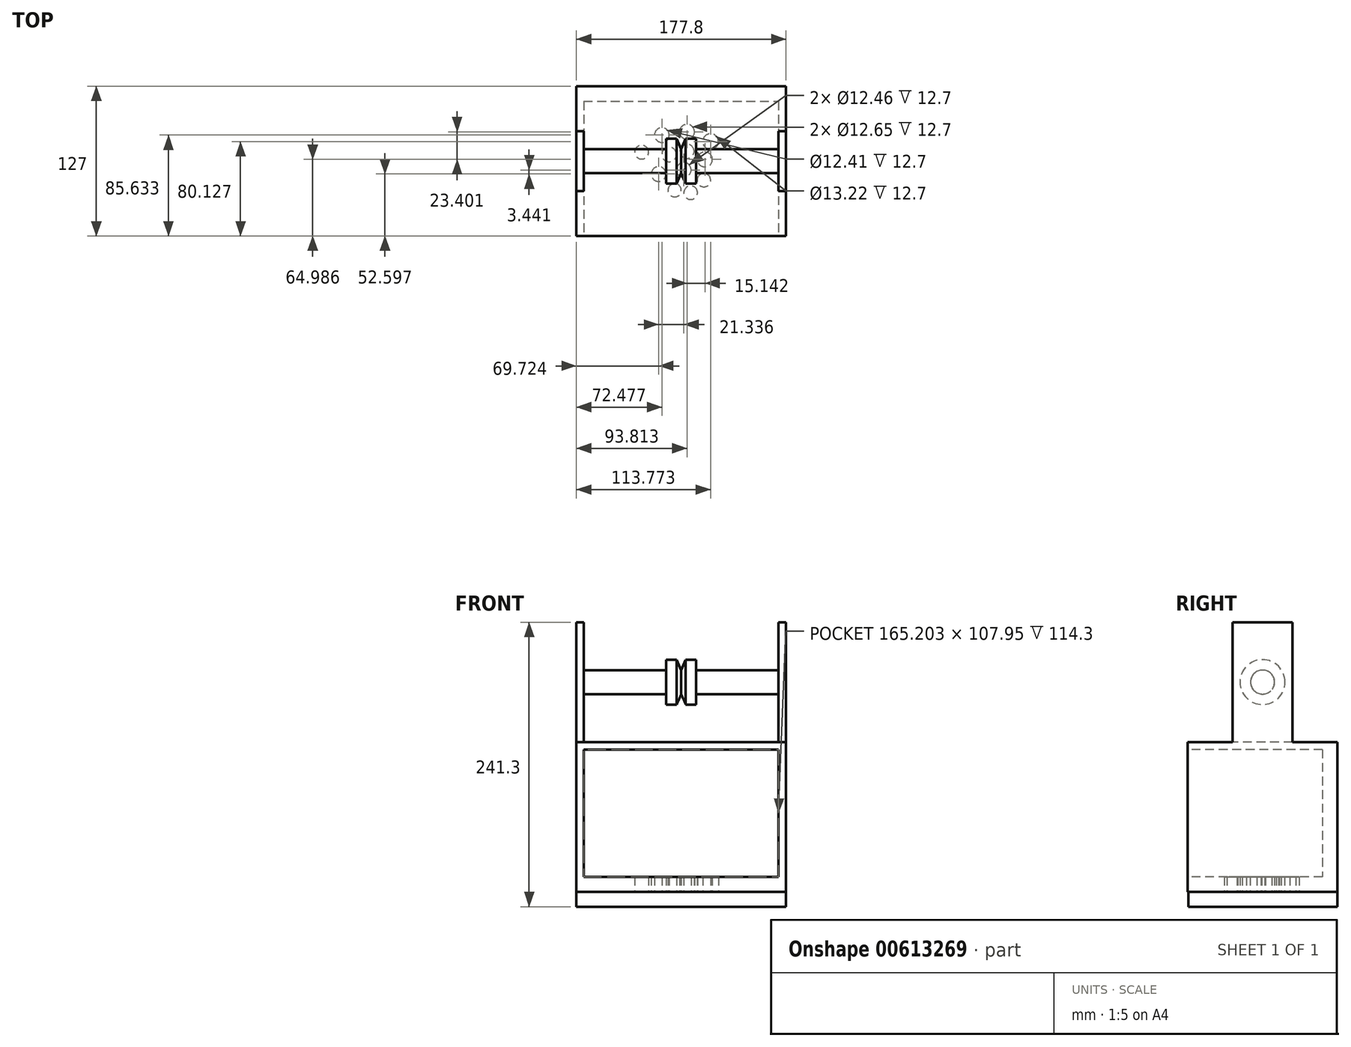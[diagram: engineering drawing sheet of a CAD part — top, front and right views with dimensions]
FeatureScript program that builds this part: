
annotation { "Feature Type Name" : "Feature", "Feature Type Description" : "" }
export const myFeature = defineFeature(function(context is Context, id is Id, definition is map)
    precondition{}
    {
        {
            var Q0;
            Q0=qCreatedBy(makeId("Front.planeOp"),FACE);
            var sketch = newSketch(context, id + "F0", { "sketchPlane" : qUnion([Q0])});
            skLineSegment(sketch, "E0", {"start": v(0, 0) * mm, "end": v(177.8, 0) * mm});
            skLineSegment(sketch, "E1", {"start": v(177.8, 0) * mm, "end": v(177.8, 228.6) * mm});
            skLineSegment(sketch, "E2", {"start": v(177.8, 228.6) * mm, "end": v(0, 228.6) * mm});
            skLineSegment(sketch, "E3", {"start": v(0, 228.6) * mm, "end": v(0, 0) * mm});
            skSolve(sketch);
        }
        {
            var Q0;
            Q0 = qSketchRegion(id + "F0", true);
            extrude(context, id + "F1", {"entities" : qUnion([Q0]), "depth" : 127 * mm, "offsetDistance" : 25.4 * mm});
        }
        {
            var Q0;
            Q0=makeQuery(id+"F1.opExtrude","SWEPT_FACE",FACE,{"disambiguationData":[OSD([sQuery(id+"F0.wireOp",EDGE,"E1")])]});
            var sketch = newSketch(context, id + "F2", { "sketchPlane" : qUnion([Q0])});
            skLineSegment(sketch, "E4.bottom", {"start": v(-127, 228.6) * mm, "end": v(-88.9, 228.6) * mm});
            skLineSegment(sketch, "E4.top", {"start": v(-127, 127) * mm, "end": v(-88.9, 127) * mm});
            skLineSegment(sketch, "E4.left", {"start": v(-127, 228.6) * mm, "end": v(-127, 127) * mm});
            skLineSegment(sketch, "E4.right", {"start": v(-88.9, 228.6) * mm, "end": v(-88.9, 127) * mm});
            skSolve(sketch);
        }
        {
            var Q0;
            Q0=makeQuery(id+"F2.imprint","IMPRINT",FACE,{"disambiguationData":[TD([[makeQuery(id+"F2.imprint","IMPRINT",EDGE,{"derivedFrom":sQuery(id+"F2.wireOp",EDGE,"E4.bottom")}),-1.0]])]});
            extrude(context, id + "F3", {"entities" : qUnion([Q0]), "operationType" : NewBodyOperationType.REMOVE, "oppositeDirection" : true, "depth" : 177.8 * mm, "offsetDistance" : 25.4 * mm});
        }
        {
            var Q0;
            Q0=makeQuery(id+"F1.opExtrude","SWEPT_FACE",FACE,{"disambiguationData":[OSD([sQuery(id+"F0.wireOp",EDGE,"E1")])]});
            var sketch = newSketch(context, id + "F4", { "sketchPlane" : qUnion([Q0])});
            skLineSegment(sketch, "E5.bottom", {"start": v(0, 228.6) * mm, "end": v(-38.1, 228.6) * mm});
            skLineSegment(sketch, "E5.top", {"start": v(0, 127) * mm, "end": v(-38.1, 127) * mm});
            skLineSegment(sketch, "E5.left", {"start": v(0, 228.6) * mm, "end": v(0, 127) * mm});
            skLineSegment(sketch, "E5.right", {"start": v(-38.1, 228.6) * mm, "end": v(-38.1, 127) * mm});
            skSolve(sketch);
        }
        {
            var Q0;
            Q0=makeQuery(id+"F4.imprint","IMPRINT",FACE,{"disambiguationData":[TD([[makeQuery(id+"F4.imprint","IMPRINT",EDGE,{"derivedFrom":sQuery(id+"F4.wireOp",EDGE,"E5.bottom")}),-1.0]])]});
            extrude(context, id + "F5", {"entities" : qUnion([Q0]), "operationType" : NewBodyOperationType.REMOVE, "oppositeDirection" : true, "depth" : 177.8 * mm, "offsetDistance" : 25.4 * mm});
        }
        {
            var Q0;
            Q0=makeQuery(id+"F1.opExtrude","SWEPT_FACE",FACE,{"disambiguationData":[OSD([sQuery(id+"F0.wireOp",EDGE,"E3")])]});
            var sketch = newSketch(context, id + "F6", { "sketchPlane" : qUnion([Q0])});
            skCircle(sketch, "E6", {"center": v(61.07, 211.22) * mm, "radius": 6.2 * mm});
            skSolve(sketch);
        }
        {
            var Q0;
            Q0=makeQuery(id+"F6.imprint","IMPRINT",FACE,{"disambiguationData":[TD([[makeQuery(id+"F6.imprint","IMPRINT",EDGE,{"derivedFrom":sQuery(id+"F6.wireOp",EDGE,"E6")}),1.0]])]});
            extrude(context, id + "F7", {"entities" : qUnion([Q0]), "operationType" : NewBodyOperationType.ADD, "oppositeDirection" : true, "depth" : 177.8 * mm, "offsetDistance" : 25.4 * mm});
        }
        {
            var Q0;
            Q0=makeQuery(id+"F1.opExtrude","SWEPT_FACE",FACE,{"disambiguationData":[OSD([sQuery(id+"F0.wireOp",EDGE,"E2")])]});
            var sketch = newSketch(context, id + "F8", { "sketchPlane" : qUnion([Q0])});
            skLineSegment(sketch, "E7", {"start": v(177.8, -38.1) * mm, "end": v(171.45, -38.1) * mm});
            skLineSegment(sketch, "E8", {"start": v(171.45, -38.1) * mm, "end": v(171.45, -88.9) * mm});
            skLineSegment(sketch, "E9", {"start": v(171.45, -88.9) * mm, "end": v(177.8, -88.9) * mm});
            skLineSegment(sketch, "E10", {"start": v(177.8, -88.9) * mm, "end": v(177.8, -38.1) * mm});
            skLineSegment(sketch, "E11", {"start": v(171.45, -38.1) * mm, "end": v(177.8, -38.1) * mm});
            skLineSegment(sketch, "E12", {"start": v(0, -88.9) * mm, "end": v(6.35, -88.9) * mm});
            skLineSegment(sketch, "E13", {"start": v(6.35, -88.9) * mm, "end": v(6.35, -38.1) * mm});
            skLineSegment(sketch, "E14", {"start": v(6.35, -38.1) * mm, "end": v(0, -38.1) * mm});
            skLineSegment(sketch, "E15", {"start": v(0, -38.1) * mm, "end": v(0, -88.9) * mm});
            skSolve(sketch);
        }
        {
            var Q0;
            {var subQ0=sQuery(id+"F8.wireOp",EDGE,"E8");Q0=makeQuery(id+"F8.imprint","IMPRINT",FACE,{"disambiguationData":[TD([[makeQuery(id+"F8.imprint","IMPRINT",EDGE,{"derivedFrom":subQ0}),-1.0]])]});}
            extrude(context, id + "F9", {"entities" : qUnion([Q0]), "operationType" : NewBodyOperationType.REMOVE, "oppositeDirection" : true, "depth" : 101.6 * mm, "offsetDistance" : 25.4 * mm});
        }
        {
            var Q0;
            Q0=makeQuery(id+"F1.opExtrude","SWEPT_FACE",FACE,{"disambiguationData":[OSD([sQuery(id+"F0.wireOp",EDGE,"E1")])]});
            var sketch = newSketch(context, id + "F10", { "sketchPlane" : qUnion([Q0])});
            skLineSegment(sketch, "E16", {"start": v(-63.5, 228.6) * mm, "end": v(-63.5, 128.6) * mm});
            skLineSegment(sketch, "E17", {"start": v(-88.9, 177.8) * mm, "end": v(-38.1, 177.8) * mm});
            skCircle(sketch, "E18", {"center": v(-63.5, 177.8) * mm, "radius": 10.2 * mm});
            skSolve(sketch);
        }
        {
            var Q0;
            {var subQ0=sQuery(id+"F10.wireOp",EDGE,"E18");var subQ1=sQuery(id+"F10.wireOp",EDGE,"E16");var subQ2=makeQuery(id+"F10.imprint","INTERSECT",VERTEX,{"disambiguationData":[OD(1.0)],"derivedFrom":[subQ1,subQ0]});Q0=makeQuery(id+"F10.imprint","IMPRINT",FACE,{"disambiguationData":[TD([[makeQuery(id+"F10.imprint","IMPRINT",EDGE,{"disambiguationData":[TD([[subQ2,-1.0]])],"derivedFrom":subQ1}),-1.0]])]});}
            var Q1;
            {var subQ0=sQuery(id+"F10.wireOp",EDGE,"E18");var subQ1=sQuery(id+"F10.wireOp",EDGE,"E16");var subQ2=makeQuery(id+"F10.imprint","INTERSECT",VERTEX,{"disambiguationData":[OD(0.0)],"derivedFrom":[subQ1,subQ0]});Q1=makeQuery(id+"F10.imprint","IMPRINT",FACE,{"disambiguationData":[TD([[makeQuery(id+"F10.imprint","IMPRINT",EDGE,{"disambiguationData":[TD([[subQ2,1.0]])],"derivedFrom":subQ1}),-1.0]])]});}
            var Q2;
            {var subQ0=sQuery(id+"F10.wireOp",EDGE,"E18");var subQ1=sQuery(id+"F10.wireOp",EDGE,"E16");var subQ2=makeQuery(id+"F10.imprint","INTERSECT",VERTEX,{"disambiguationData":[OD(0.0)],"derivedFrom":[subQ1,subQ0]});Q2=makeQuery(id+"F10.imprint","IMPRINT",FACE,{"disambiguationData":[TD([[makeQuery(id+"F10.imprint","IMPRINT",EDGE,{"disambiguationData":[TD([[subQ2,1.0]])],"derivedFrom":subQ1}),1.0]])]});}
            var Q3;
            {var subQ0=sQuery(id+"F10.wireOp",EDGE,"E18");var subQ1=sQuery(id+"F10.wireOp",EDGE,"E16");var subQ2=makeQuery(id+"F10.imprint","INTERSECT",VERTEX,{"disambiguationData":[OD(1.0)],"derivedFrom":[subQ1,subQ0]});Q3=makeQuery(id+"F10.imprint","IMPRINT",FACE,{"disambiguationData":[TD([[makeQuery(id+"F10.imprint","IMPRINT",EDGE,{"disambiguationData":[TD([[subQ2,-1.0]])],"derivedFrom":subQ1}),1.0]])]});}
            extrude(context, id + "F11", {"entities" : qUnion([Q0, Q1, Q2, Q3]), "operationType" : NewBodyOperationType.ADD, "oppositeDirection" : true, "depth" : 174.5 * mm, "offsetDistance" : 25.4 * mm});
        }
        {
            var Q0;
            Q0=makeQuery(id+"F1.opExtrude","CAP_FACE",FACE,{"disambiguationData":[OSD([sQuery(id+"F0.wireOp",EDGE,"E0"),sQuery(id+"F0.wireOp",EDGE,"E1"),sQuery(id+"F0.wireOp",EDGE,"E2"),sQuery(id+"F0.wireOp",EDGE,"E3")])],"isStart":false});
            var sketch = newSketch(context, id + "F12", { "sketchPlane" : qUnion([Q0])});
            skLineSegment(sketch, "E19", {"start": v(0, 127) * mm, "end": v(0, 120.65) * mm});
            skLineSegment(sketch, "E20", {"start": v(0, 120.65) * mm, "end": v(177.8, 120.65) * mm});
            skLineSegment(sketch, "E21", {"start": v(177.8, 120.65) * mm, "end": v(177.8, 127) * mm});
            skLineSegment(sketch, "E22", {"start": v(177.8, 127) * mm, "end": v(0, 127) * mm});
            skLineSegment(sketch, "E23", {"start": v(0, 0) * mm, "end": v(0, 12.7) * mm});
            skLineSegment(sketch, "E24", {"start": v(0, 12.7) * mm, "end": v(177.8, 12.7) * mm});
            skLineSegment(sketch, "E25", {"start": v(177.8, 12.7) * mm, "end": v(177.8, 0) * mm});
            skLineSegment(sketch, "E26", {"start": v(177.8, 0) * mm, "end": v(0, 0) * mm});
            skLineSegment(sketch, "E27", {"start": v(171.35, 127) * mm, "end": v(171.35, 12.7) * mm});
            skLineSegment(sketch, "E28", {"start": v(6.15, 127) * mm, "end": v(6.15, 12.7) * mm});
            skSolve(sketch);
        }
        {
            var Q0;
            {var subQ0=sQuery(id+"F12.wireOp",EDGE,"E28");var subQ1=sQuery(id+"F12.wireOp",EDGE,"E20");var subQ2=makeQuery(id+"F12.imprint","INTERSECT",VERTEX,{"derivedFrom":[subQ1,subQ0]});Q0=makeQuery(id+"F12.imprint","IMPRINT",FACE,{"disambiguationData":[TD([[makeQuery(id+"F12.imprint","IMPRINT",EDGE,{"disambiguationData":[TD([[subQ2,-1.0]])],"derivedFrom":subQ1}),-1.0]])]});}
            extrude(context, id + "F13", {"entities" : qUnion([Q0]), "operationType" : NewBodyOperationType.REMOVE, "oppositeDirection" : true, "depth" : 114.3 * mm, "offsetDistance" : 25.4 * mm});
        }
        {
            var Q0;
            Q0=makeQuery(id+"F1.opExtrude","SWEPT_FACE",FACE,{"disambiguationData":[OSD([sQuery(id+"F0.wireOp",EDGE,"E0")])]});
            var sketch = newSketch(context, id + "F14", { "sketchPlane" : qUnion([Q0])});
            skSolve(sketch);
        }
        {
            var Q0;
            {var subQ0=sQuery(id+"F0.wireOp",EDGE,"E0");Q0=makeQuery(id+"F14.imprint","IMPRINT",FACE,{"disambiguationData":[TD([[makeQuery(id+"F14.imprint","IMPRINT",EDGE,{"derivedFrom":makeQuery(id+"F1.opExtrude","CAP_EDGE",EDGE,{"disambiguationData":[OSD([subQ0])],"isStart":true})}),1.0]])]});}
            var sketch = newSketch(context, id + "F15", { "sketchPlane" : qUnion([Q0])});
            skCircle(sketch, "E29", {"center": v(83.32, 88.2) * mm, "radius": 5.6 * mm});
            skSolve(sketch);
        }
        {
            var Q0;
            Q0 = qSketchRegion(id + "F15", true);
            extrude(context, id + "F16", {"entities" : qUnion([Q0]), "operationType" : NewBodyOperationType.REMOVE, "oppositeDirection" : true, "depth" : 25.4 * mm, "offsetDistance" : 25.4 * mm});
        }
        {
            var Q0;
            {var subQ0=sQuery(id+"F0.wireOp",EDGE,"E0");Q0=makeQuery(id+"F14.imprint","IMPRINT",FACE,{"disambiguationData":[TD([[makeQuery(id+"F14.imprint","IMPRINT",EDGE,{"derivedFrom":makeQuery(id+"F1.opExtrude","CAP_EDGE",EDGE,{"disambiguationData":[OSD([subQ0])],"isStart":true})}),1.0]])]});}
            var sketch = newSketch(context, id + "F17", { "sketchPlane" : qUnion([Q0])});
            skCircle(sketch, "E30", {"center": v(108.1, 79.6) * mm, "radius": 5.68 * mm});
            skSolve(sketch);
        }
        {
            var Q0;
            Q0 = qSketchRegion(id + "F17", true);
            extrude(context, id + "F18", {"entities" : qUnion([Q0]), "operationType" : NewBodyOperationType.REMOVE, "oppositeDirection" : true, "depth" : 25.4 * mm, "offsetDistance" : 25.4 * mm});
        }
        {
            var Q0;
            {var subQ0=sQuery(id+"F0.wireOp",EDGE,"E0");Q0=makeQuery(id+"F14.imprint","IMPRINT",FACE,{"disambiguationData":[TD([[makeQuery(id+"F14.imprint","IMPRINT",EDGE,{"derivedFrom":makeQuery(id+"F1.opExtrude","CAP_EDGE",EDGE,{"disambiguationData":[OSD([subQ0])],"isStart":true})}),1.0]])]});}
            var sketch = newSketch(context, id + "F19", { "sketchPlane" : qUnion([Q0])});
            skCircle(sketch, "E31", {"center": v(91.06, 70.96) * mm, "radius": 6.23 * mm});
            skSolve(sketch);
        }
        {
            var Q0;
            Q0 = qSketchRegion(id + "F19", true);
            extrude(context, id + "F20", {"entities" : qUnion([Q0]), "operationType" : NewBodyOperationType.REMOVE, "oppositeDirection" : true, "depth" : 25.4 * mm, "offsetDistance" : 25.4 * mm});
        }
        {
            var Q0;
            {var subQ0=sQuery(id+"F0.wireOp",EDGE,"E0");Q0=makeQuery(id+"F14.imprint","IMPRINT",FACE,{"disambiguationData":[TD([[makeQuery(id+"F14.imprint","IMPRINT",EDGE,{"derivedFrom":makeQuery(id+"F1.opExtrude","CAP_EDGE",EDGE,{"disambiguationData":[OSD([subQ0])],"isStart":true})}),1.0]])]});}
            var sketch = newSketch(context, id + "F21", { "sketchPlane" : qUnion([Q0])});
            skCircle(sketch, "E32", {"center": v(69.72, 74.4) * mm, "radius": 6.23 * mm});
            skSolve(sketch);
        }
        {
            var Q0;
            Q0 = qSketchRegion(id + "F21", true);
            extrude(context, id + "F22", {"entities" : qUnion([Q0]), "operationType" : NewBodyOperationType.REMOVE, "oppositeDirection" : true, "depth" : 25.4 * mm, "offsetDistance" : 25.4 * mm});
        }
        {
            var Q0;
            {var subQ0=sQuery(id+"F0.wireOp",EDGE,"E0");Q0=makeQuery(id+"F14.imprint","IMPRINT",FACE,{"disambiguationData":[TD([[makeQuery(id+"F14.imprint","IMPRINT",EDGE,{"derivedFrom":makeQuery(id+"F1.opExtrude","CAP_EDGE",EDGE,{"disambiguationData":[OSD([subQ0])],"isStart":true})}),1.0]])]});}
            var sketch = newSketch(context, id + "F23", { "sketchPlane" : qUnion([Q0])});
            skCircle(sketch, "E33", {"center": v(78.67, 57.88) * mm, "radius": 6.2 * mm});
            skSolve(sketch);
        }
        {
            var Q0;
            Q0 = qSketchRegion(id + "F23", true);
            extrude(context, id + "F24", {"entities" : qUnion([Q0]), "operationType" : NewBodyOperationType.REMOVE, "oppositeDirection" : true, "depth" : 25.4 * mm, "offsetDistance" : 25.4 * mm});
        }
        {
            var Q0;
            {var subQ0=sQuery(id+"F0.wireOp",EDGE,"E0");Q0=makeQuery(id+"F14.imprint","IMPRINT",FACE,{"disambiguationData":[TD([[makeQuery(id+"F14.imprint","IMPRINT",EDGE,{"derivedFrom":makeQuery(id+"F1.opExtrude","CAP_EDGE",EDGE,{"disambiguationData":[OSD([subQ0])],"isStart":true})}),1.0]])]});}
            var sketch = newSketch(context, id + "F25", { "sketchPlane" : qUnion([Q0])});
            skCircle(sketch, "E34", {"center": v(108.96, 62.01) * mm, "radius": 6.33 * mm});
            skSolve(sketch);
        }
        {
            var Q0;
            Q0 = qSketchRegion(id + "F25", true);
            extrude(context, id + "F26", {"entities" : qUnion([Q0]), "operationType" : NewBodyOperationType.REMOVE, "oppositeDirection" : true, "depth" : 25.4 * mm, "offsetDistance" : 25.4 * mm});
        }
        {
            var Q0;
            {var subQ0=sQuery(id+"F0.wireOp",EDGE,"E0");Q0=makeQuery(id+"F14.imprint","IMPRINT",FACE,{"disambiguationData":[TD([[makeQuery(id+"F14.imprint","IMPRINT",EDGE,{"derivedFrom":makeQuery(id+"F1.opExtrude","CAP_EDGE",EDGE,{"disambiguationData":[OSD([subQ0])],"isStart":true})}),1.0]])]});}
            var sketch = newSketch(context, id + "F27", { "sketchPlane" : qUnion([Q0])});
            skCircle(sketch, "E35", {"center": v(96.91, 90.23) * mm, "radius": 5.77 * mm});
            skSolve(sketch);
        }
        {
            var Q0;
            Q0 = qSketchRegion(id + "F27", true);
            extrude(context, id + "F28", {"entities" : qUnion([Q0]), "operationType" : NewBodyOperationType.REMOVE, "oppositeDirection" : true, "depth" : 25.4 * mm, "offsetDistance" : 25.4 * mm});
        }
        {
            var Q0;
            {var subQ0=sQuery(id+"F0.wireOp",EDGE,"E0");Q0=makeQuery(id+"F14.imprint","IMPRINT",FACE,{"disambiguationData":[TD([[makeQuery(id+"F14.imprint","IMPRINT",EDGE,{"derivedFrom":makeQuery(id+"F1.opExtrude","CAP_EDGE",EDGE,{"disambiguationData":[OSD([subQ0])],"isStart":true})}),1.0]])]});}
            var sketch = newSketch(context, id + "F29", { "sketchPlane" : qUnion([Q0])});
            skCircle(sketch, "E36", {"center": v(93.81, 55.13) * mm, "radius": 6 * mm});
            skSolve(sketch);
        }
        {
            var Q0;
            Q0 = qSketchRegion(id + "F29", true);
            extrude(context, id + "F30", {"entities" : qUnion([Q0]), "operationType" : NewBodyOperationType.REMOVE, "oppositeDirection" : true, "depth" : 25.4 * mm, "offsetDistance" : 25.4 * mm});
        }
        {
            var Q0;
            {var subQ0=sQuery(id+"F0.wireOp",EDGE,"E0");Q0=makeQuery(id+"F14.imprint","IMPRINT",FACE,{"disambiguationData":[TD([[makeQuery(id+"F14.imprint","IMPRINT",EDGE,{"derivedFrom":makeQuery(id+"F1.opExtrude","CAP_EDGE",EDGE,{"disambiguationData":[OSD([subQ0])],"isStart":true})}),1.0]])]});}
            var sketch = newSketch(context, id + "F31", { "sketchPlane" : qUnion([Q0])});
            skCircle(sketch, "E37", {"center": v(55.27, 55.82) * mm, "radius": 5.9 * mm});
            skSolve(sketch);
        }
        {
            var Q0;
            Q0 = qSketchRegion(id + "F31", true);
            extrude(context, id + "F32", {"entities" : qUnion([Q0]), "operationType" : NewBodyOperationType.REMOVE, "oppositeDirection" : true, "depth" : 25.4 * mm, "offsetDistance" : 25.4 * mm});
        }
        {
            var Q0;
            {var subQ0=sQuery(id+"F0.wireOp",EDGE,"E0");Q0=makeQuery(id+"F14.imprint","IMPRINT",FACE,{"disambiguationData":[TD([[makeQuery(id+"F14.imprint","IMPRINT",EDGE,{"derivedFrom":makeQuery(id+"F1.opExtrude","CAP_EDGE",EDGE,{"disambiguationData":[OSD([subQ0])],"isStart":true})}),1.0]])]});}
            var sketch = newSketch(context, id + "F33", { "sketchPlane" : qUnion([Q0])});
            skCircle(sketch, "E38", {"center": v(72.48, 41.37) * mm, "radius": 6.2 * mm});
            skSolve(sketch);
        }
        {
            var Q0;
            Q0 = qSketchRegion(id + "F33", true);
            extrude(context, id + "F34", {"entities" : qUnion([Q0]), "operationType" : NewBodyOperationType.REMOVE, "oppositeDirection" : true, "depth" : 25.4 * mm, "offsetDistance" : 25.4 * mm});
        }
        {
            var Q0;
            {var subQ0=sQuery(id+"F0.wireOp",EDGE,"E0");Q0=makeQuery(id+"F14.imprint","IMPRINT",FACE,{"disambiguationData":[TD([[makeQuery(id+"F14.imprint","IMPRINT",EDGE,{"derivedFrom":makeQuery(id+"F1.opExtrude","CAP_EDGE",EDGE,{"disambiguationData":[OSD([subQ0])],"isStart":true})}),1.0]])]});}
            var sketch = newSketch(context, id + "F35", { "sketchPlane" : qUnion([Q0])});
            skCircle(sketch, "E39", {"center": v(93.81, 38.61) * mm, "radius": 6.33 * mm});
            skSolve(sketch);
        }
        {
            var Q0;
            Q0 = qSketchRegion(id + "F35", true);
            extrude(context, id + "F36", {"entities" : qUnion([Q0]), "operationType" : NewBodyOperationType.REMOVE, "oppositeDirection" : true, "depth" : 25.4 * mm, "offsetDistance" : 25.4 * mm});
        }
        {
            var Q0;
            {var subQ0=sQuery(id+"F0.wireOp",EDGE,"E0");Q0=makeQuery(id+"F14.imprint","IMPRINT",FACE,{"disambiguationData":[TD([[makeQuery(id+"F14.imprint","IMPRINT",EDGE,{"derivedFrom":makeQuery(id+"F1.opExtrude","CAP_EDGE",EDGE,{"disambiguationData":[OSD([subQ0])],"isStart":true})}),1.0]])]});}
            var sketch = newSketch(context, id + "F37", { "sketchPlane" : qUnion([Q0])});
            skCircle(sketch, "E40", {"center": v(113.77, 46.87) * mm, "radius": 6.61 * mm});
            skSolve(sketch);
        }
        {
            var Q0;
            Q0 = qSketchRegion(id + "F37", true);
            extrude(context, id + "F38", {"entities" : qUnion([Q0]), "operationType" : NewBodyOperationType.REMOVE, "oppositeDirection" : true, "depth" : 25.4 * mm, "offsetDistance" : 25.4 * mm});
        }
        {
            var Q0;
            Q0=qCreatedBy(makeId("Right.planeOp"),FACE);
            cPlane(context, id + "F39", {"entities" : qUnion([Q0]), "cplaneType" : CPlaneType.OFFSET, "offset" : 88.9 * mm, "width" : 152.4 * mm, "height" : 152.4 * mm});
        }
        {
            var Q0;
            Q0=qCreatedBy(id+"F39.planeOp",FACE);
            var sketch = newSketch(context, id + "F40", { "sketchPlane" : qUnion([Q0])});
            skCircle(sketch, "E41.0", {"center": v(-63.5, 177.8) * mm, "radius": 10.2 * mm});
            skCircle(sketch, "E42", {"center": v(-63.5, 177.8) * mm, "radius": 19.05 * mm});
            skSolve(sketch);
        }
        {
            var Q0;
            Q0 = qSketchRegion(id + "F40", true);
            extrude(context, id + "F41", {"entities" : qUnion([Q0]), "operationType" : NewBodyOperationType.ADD, "endBound" : BoundingType.SYMMETRIC, "depth" : 25.4 * mm, "offsetDistance" : 25.4 * mm});
        }
        {
            var Q0;
            {var subQ0=sQuery(id+"F0.wireOp",EDGE,"E0");Q0=makeQuery(id+"F14.imprint","IMPRINT",FACE,{"disambiguationData":[TD([[makeQuery(id+"F14.imprint","IMPRINT",EDGE,{"derivedFrom":makeQuery(id+"F1.opExtrude","CAP_EDGE",EDGE,{"disambiguationData":[OSD([subQ0])],"isStart":true})}),1.0]])]});}
            var sketch = newSketch(context, id + "F42", { "sketchPlane" : qUnion([Q0])});
            skLineSegment(sketch, "E43", {"start": v(0, 0) * mm, "end": v(0, 126.4) * mm});
            skLineSegment(sketch, "E44", {"start": v(0, 126.4) * mm, "end": v(177.61, 126.4) * mm});
            skLineSegment(sketch, "E45", {"start": v(177.61, 126.4) * mm, "end": v(177.61, 0) * mm});
            skLineSegment(sketch, "E46", {"start": v(177.61, 0) * mm, "end": v(0, 0) * mm});
            skSolve(sketch);
        }
        {
            var Q0;
            Q0 = qSketchRegion(id + "F42", true);
            extrude(context, id + "F43", {"entities" : qUnion([Q0]), "operationType" : NewBodyOperationType.ADD, "depth" : 12.7 * mm, "offsetDistance" : 25.4 * mm});
        }
        {
            var Q0;
            Q0=qCreatedBy(makeId("Front.planeOp"),FACE);
            cPlane(context, id + "F44", {"entities" : qUnion([Q0]), "cplaneType" : CPlaneType.OFFSET, "offset" : 63.5 * mm, "width" : 152.4 * mm, "height" : 152.4 * mm});
        }
        {
            var Q0;
            Q0=qCreatedBy(id+"F44.planeOp",FACE);
            var sketch = newSketch(context, id + "F45", { "sketchPlane" : qUnion([Q0])});
            skLineSegment(sketch, "E47", {"start": v(92.7, 196.85) * mm, "end": v(88.87, 187.96) * mm});
            skLineSegment(sketch, "E48", {"start": v(88.87, 187.96) * mm, "end": v(85.06, 196.85) * mm});
            skLineSegment(sketch, "E49", {"start": v(75.82, 177.8) * mm, "end": v(101.6, 177.8) * mm});
            skLineSegment(sketch, "E50", {"start": v(85.06, 196.85) * mm, "end": v(92.71, 196.85) * mm});
            skSolve(sketch);
        }
        {
            var Q0;
            Q0 = qSketchRegion(id + "F45", true);
            var Q1;
            Q1=sQuery(id+"F45.wireOp",EDGE,"E49");
            revolve(context, id + "F46", {"operationType" : NewBodyOperationType.REMOVE, "entities" : qUnion([Q0]), "axis" : qUnion([Q1]), "revolveType" : RevolveType.FULL, "oppositeDirection" : true});
        }
    });
